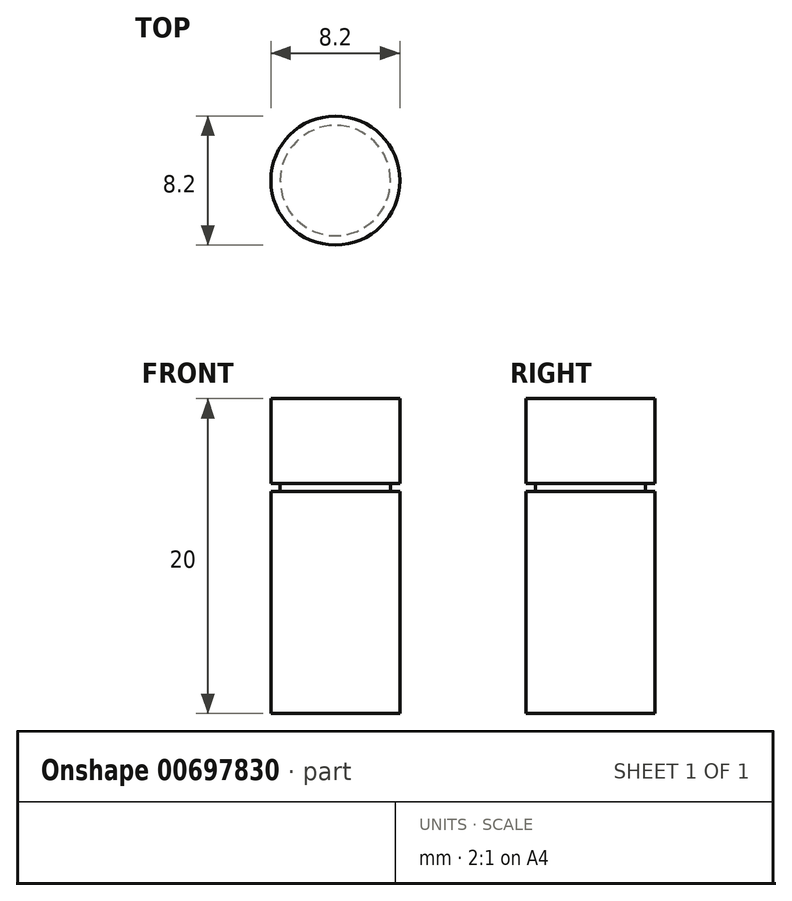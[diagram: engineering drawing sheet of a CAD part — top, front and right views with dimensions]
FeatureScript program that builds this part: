
annotation { "Feature Type Name" : "Feature", "Feature Type Description" : "" }
export const myFeature = defineFeature(function(context is Context, id is Id, definition is map)
    precondition{}
    {
        {
            var Q0;
            Q0=qCreatedBy(makeId("Top.planeOp"),FACE);
            var sketch = newSketch(context, id + "F0", { "sketchPlane" : qUnion([Q0])});
            skCircle(sketch, "E0", {"center": v(0, 0) * mm, "radius": 4.1 * mm});
            skSolve(sketch);
        }
        {
            var Q0;
            Q0 = qSketchRegion(id + "F0", true);
            extrude(context, id + "F1", {"entities" : qUnion([Q0]), "depth" : 20 * mm, "offsetDistance" : 25 * mm});
        }
        {
            var Q0;
            Q0=qCreatedBy(makeId("Front.planeOp"),FACE);
            var sketch = newSketch(context, id + "F2", { "sketchPlane" : qUnion([Q0])});
            skLineSegment(sketch, "E1", {"start": v(4.1, 20) * mm, "end": v(4.1, 14.6) * mm, "construction": true});
            skLineSegment(sketch, "E2.bottom", {"start": v(4.1, 14.6) * mm, "end": v(3.5, 14.6) * mm});
            skLineSegment(sketch, "E2.top", {"start": v(4.1, 14.1) * mm, "end": v(3.5, 14.1) * mm});
            skLineSegment(sketch, "E2.left", {"start": v(4.1, 14.6) * mm, "end": v(4.1, 14.1) * mm});
            skLineSegment(sketch, "E2.right", {"start": v(3.5, 14.6) * mm, "end": v(3.5, 14.1) * mm});
            skSolve(sketch);
        }
        {
            var Q0;
            Q0 = qSketchRegion(id + "F2", true);
            var Q1;
            Q1=makeQuery(id+"F1.opExtrude","SWEPT_FACE",FACE,{"disambiguationData":[OSD([sQuery(id+"F0.wireOp",EDGE,"E0")])]});
            revolve(context, id + "F3", {"operationType" : NewBodyOperationType.REMOVE, "entities" : qUnion([Q0]), "axis" : qUnion([Q1]), "revolveType" : RevolveType.FULL, "oppositeDirection" : true});
        }
    });
